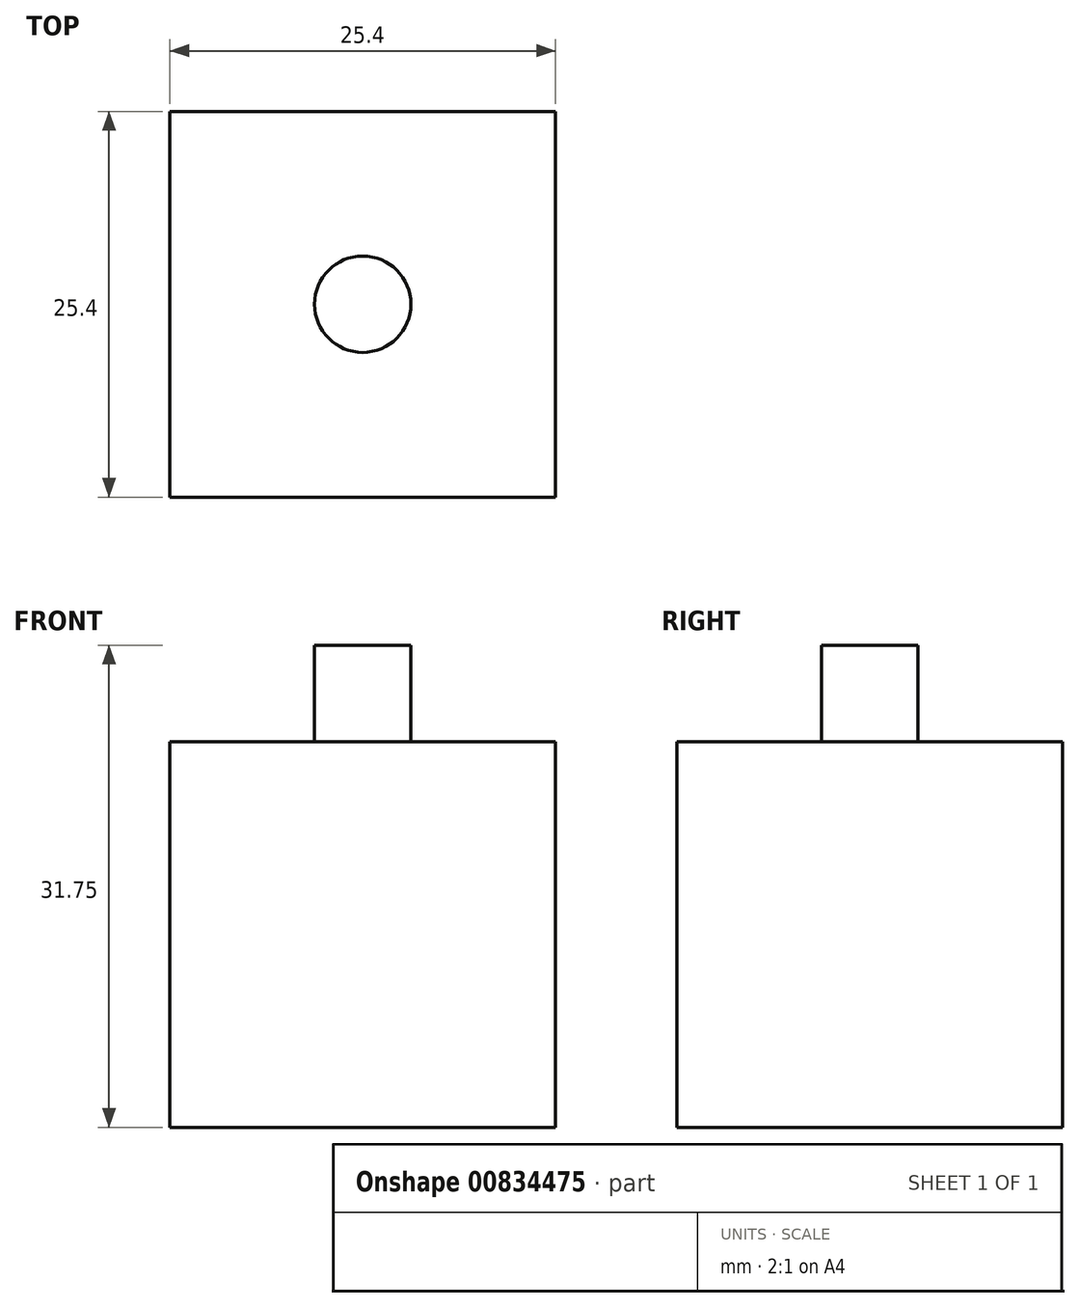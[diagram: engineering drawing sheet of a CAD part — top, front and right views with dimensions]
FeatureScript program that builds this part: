
annotation { "Feature Type Name" : "Feature", "Feature Type Description" : "" }
export const myFeature = defineFeature(function(context is Context, id is Id, definition is map)
    precondition{}
    {
        {
            var Q0;
            Q0=qCreatedBy(makeId("Top.planeOp"),FACE);
            var sketch = newSketch(context, id + "F0", { "sketchPlane" : qUnion([Q0])});
            skLineSegment(sketch, "E0.bottom", {"start": v(0, 0) * mm, "end": v(25.4, 0) * mm});
            skLineSegment(sketch, "E0.top", {"start": v(0, 25.4) * mm, "end": v(25.4, 25.4) * mm});
            skLineSegment(sketch, "E0.left", {"start": v(0, 0) * mm, "end": v(0, 25.4) * mm});
            skLineSegment(sketch, "E0.right", {"start": v(25.4, 0) * mm, "end": v(25.4, 25.4) * mm});
            skSolve(sketch);
        }
        {
            var Q0;
            Q0=makeQuery(id+"F0.imprint","IMPRINT",FACE,{"disambiguationData":[TD([[makeQuery(id+"F0.imprint","IMPRINT",EDGE,{"derivedFrom":sQuery(id+"F0.wireOp",EDGE,"E0.bottom")}),1.0]])]});
            extrude(context, id + "F1", {"entities" : qUnion([Q0]), "depth" : 25.4 * mm, "offsetDistance" : 25.4 * mm});
        }
        {
            var Q0;
            Q0=makeQuery(id+"F1.opExtrude","CAP_FACE",FACE,{"disambiguationData":[OSD([sQuery(id+"F0.wireOp",EDGE,"E0.bottom"),sQuery(id+"F0.wireOp",EDGE,"E0.top"),sQuery(id+"F0.wireOp",EDGE,"E0.left"),sQuery(id+"F0.wireOp",EDGE,"E0.right")])],"isStart":false});
            var sketch = newSketch(context, id + "F2", { "sketchPlane" : qUnion([Q0])});
            skCircle(sketch, "E1", {"center": v(12.7, 12.7) * mm, "radius": 3.17 * mm});
            skPoint(sketch, "E1.centerSnap0", {"position": v(12.7, 0) * mm});
            skSolve(sketch);
        }
        {
            var Q0;
            Q0=makeQuery(id+"F2.imprint","IMPRINT",FACE,{"disambiguationData":[TD([[makeQuery(id+"F2.imprint","IMPRINT",EDGE,{"derivedFrom":sQuery(id+"F2.wireOp",EDGE,"E1")}),1.0]])]});
            extrude(context, id + "F3", {"entities" : qUnion([Q0]), "operationType" : NewBodyOperationType.ADD, "depth" : 6.35 * mm, "offsetDistance" : 25.4 * mm});
        }
    });
